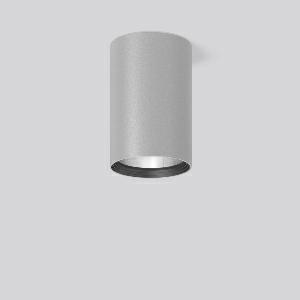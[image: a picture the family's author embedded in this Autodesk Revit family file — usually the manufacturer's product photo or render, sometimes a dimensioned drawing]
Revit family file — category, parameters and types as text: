
# Revit family: heledon_maxi_a_931233_004_76_e8a8
name_source: partatom
category: Lighting Fixtures
units: mm (PartAtom-declared; Revit-internal decimal feet)

## family parameters
Cut with Voids When Loaded = No
Host = Face
Light Source = No
Part Type = Normal
Room Calculation Point = No
Round Connector Dimension = Use Diameter
Shared = No

## types (1)
- HELEDON maxi A (1 x LED Modul 932 fresh meat, 2050 lm, 3200)
    Apparent Load = 33 VA
    Approval mark = CE
    CIE Flux Codes = 96 100 100 100 100
    Color Rendering = 90
    Color Temperature = 3200
    Default Elevation = 1800 mm
    Description = Series: HELEDON maxi
Cylindrical surface-mounted downlight. Housing: die-cast aluminium, powder-coated. Internal ceiling frame polycarbonate with bayonet mounting. Black plastic ring and recessed LED to prevent glare from the side. Optical assembly with reflector made of MIRO-Silver with 98% total light reflection for outstanding efficiency - can be changed without tools. Special LED for illumination of meat included. Suitable for Ceiling mounting. Easy installation with a separate ceiling frame with bayonet mounting and plug connection. Driver integrated. Connected via plug-in connector. High quality converter without flickering and stroboscopic effect. The following accessories can be mounted without use of tools: interchangeable lenses, decorative glasses, honeycomb louvre, clear and frosted diffusers, white interchangeable plastic ring. 
Colour: silver
Diameter: 123 mm
Height: 183 mm
Lamp: LED
Socket: without socket
Colour temperature: fresh meat
System power: 33 W
Rated luminous flux: 2050 lm
Luminous efficiency: 62 lm/W
Control gear: Converter, dimmable, DALI
Protection class: I
Type of protection: IP 20
    Height = 183 mm
    Lamp = 1 x LED Modul 932 fresh meat
    Lamp Light Flux = 2050 lm
    Lamp count = 1
    Length = 123 mm
    Lifetime = 50000 h
    Luminous efficacy = 62 lm/W
    Manufacturer = RZB
    ModVariant = No
    Model = 931233.004.76
    Mounting Place = Ceiling
    Mounting Type = Surface mounted
    Number of Poles = 1
    OnlyDefault = Yes
    Power Factor = 1
    Product Name = HELEDON maxi A
    Product group = Surface mounted downlights
    ProductGroupID = 302
    Protection Class = Protection class I
    Protection Degree = IP 20
    RLX_Detail_Level = 1
    RLX_Emergency_Light_Flux = 0 lm
    RLX_Emergency_Type = 0
    RLX_Emergency_Type_DB = No
    RlxData = <blob elided: 98509 chars, md5=42e68c14>
    Socket = socket
    Standby Power = 0 W
    System Light Flux = 2050 lm
    System Power = 33 W
    Type Comments = Product without accessories
    Type Image = 931192.004.jpg
    URL = http://relux.com
    VarID = ---
    Voltage = 230 V
    Voltage Range = 220-240 V
    Weight = 0.00 kg
    Width = 0 mm  [stored 0 ft]

note: [stored X ft] marks values corroborated as IEEE doubles in the binary element streams (Revit-internal decimal feet)

## geometry (parser evidence)
native form markers: Blend x4, Sweep x12
no freeform markers — native parametric forms only
